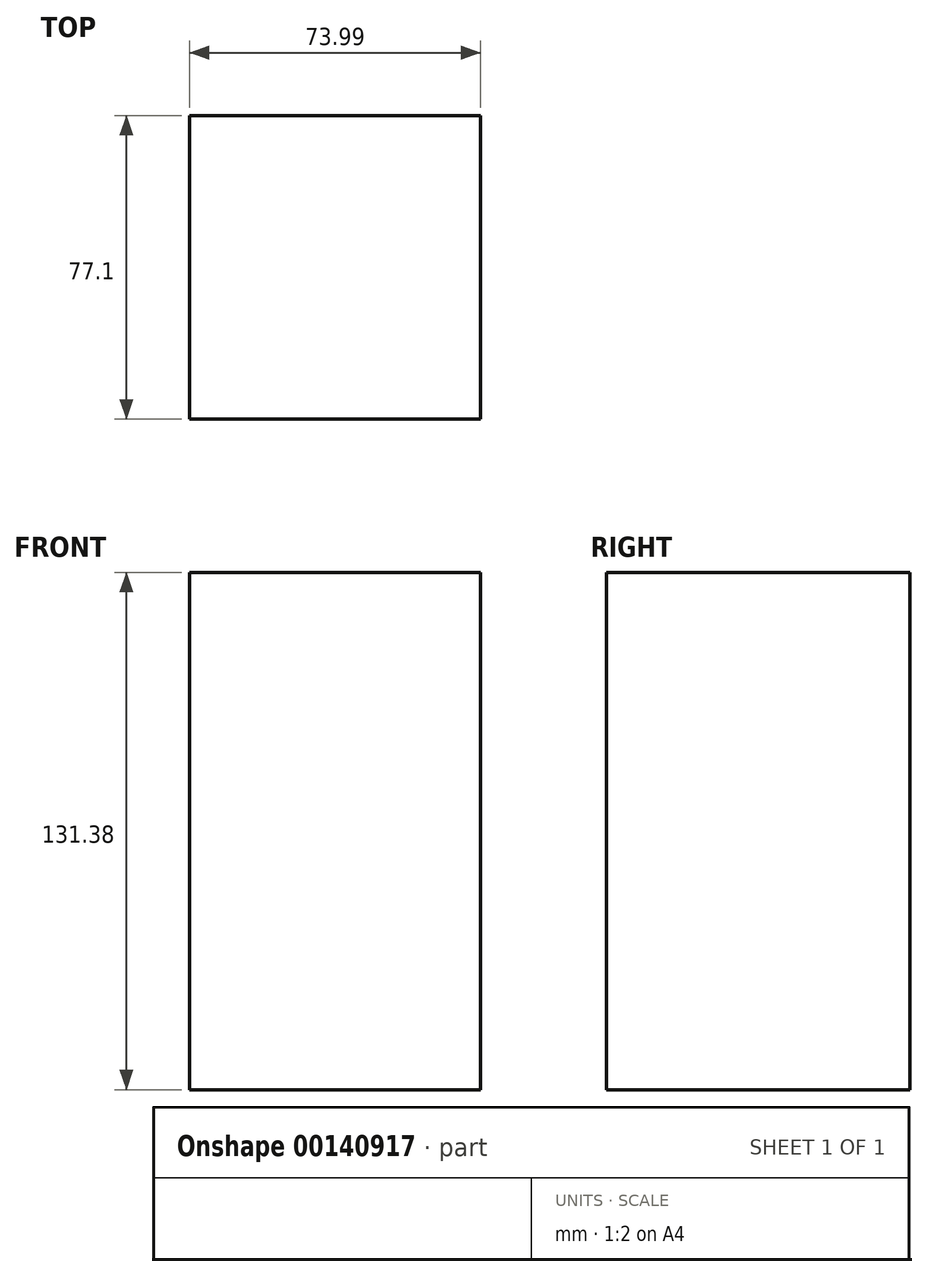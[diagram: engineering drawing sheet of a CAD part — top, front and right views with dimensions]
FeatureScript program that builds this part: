
annotation { "Feature Type Name" : "Feature", "Feature Type Description" : "" }
export const myFeature = defineFeature(function(context is Context, id is Id, definition is map)
    precondition{}
    {
        {
            var Q0;
            Q0=qCreatedBy(makeId("Front.planeOp"),FACE);
            var sketch = newSketch(context, id + "F0", { "sketchPlane" : qUnion([Q0])});
            skLineSegment(sketch, "E0.bottom", {"start": v(-113.77, 27.71) * mm, "end": v(-39.78, 27.71) * mm});
            skLineSegment(sketch, "E0.top", {"start": v(-113.77, 133.69) * mm, "end": v(-39.78, 133.69) * mm});
            skLineSegment(sketch, "E0.left", {"start": v(-113.77, 27.71) * mm, "end": v(-113.77, 133.69) * mm});
            skLineSegment(sketch, "E0.right", {"start": v(-39.78, 27.71) * mm, "end": v(-39.78, 133.69) * mm});
            skSolve(sketch);
        }
        {
            var Q0;
            Q0=makeQuery(id+"F0.imprint","IMPRINT",FACE,{"disambiguationData":[TD([[makeQuery(id+"F0.imprint","IMPRINT",EDGE,{"derivedFrom":sQuery(id+"F0.wireOp",EDGE,"E0.bottom")}),1.0]])]});
            extrude(context, id + "F1", {"entities" : qUnion([Q0]), "depth" : 77.1 * mm});
        }
        {
            var Q0;
            Q0=makeQuery(id+"F1.opExtrude","SWEPT_FACE",FACE,{"disambiguationData":[OSD([sQuery(id+"F0.wireOp",EDGE,"E0.top")])]});
            var sketch = newSketch(context, id + "F3", { "sketchPlane" : qUnion([Q0])});
            skCircle(sketch, "E1", {"center": v(-70.06, -38.4) * mm, "radius": 171.85 * mm});
            skSolve(sketch);
        }
        {
            var Q0;
            {var subQ0=sQuery(id+"F0.wireOp",EDGE,"E0.top");Q0=makeQuery(id+"F3.imprint","IMPRINT",FACE,{"disambiguationData":[TD([[makeQuery(id+"F3.imprint","IMPRINT",EDGE,{"derivedFrom":makeQuery(id+"F1.opExtrude","CAP_EDGE",EDGE,{"disambiguationData":[OSD([subQ0])],"isStart":true})}),-1.0]])]});}
            extrude(context, id + "F2", {"entities" : qUnion([Q0]), "operationType" : NewBodyOperationType.ADD, "depth" : 25.4 * mm});
        }
    });
